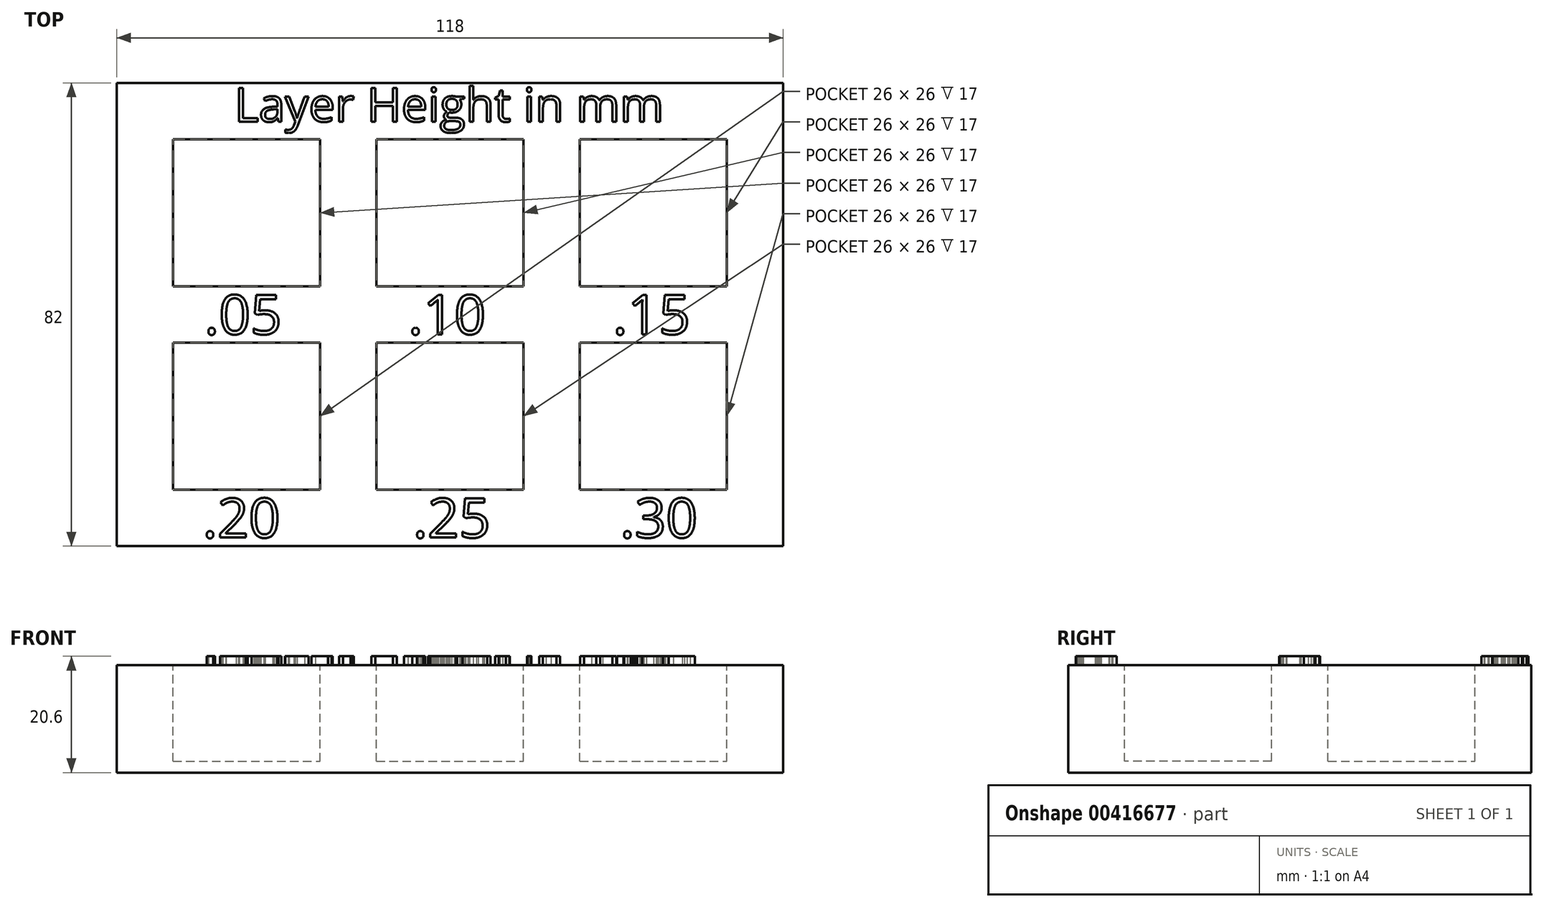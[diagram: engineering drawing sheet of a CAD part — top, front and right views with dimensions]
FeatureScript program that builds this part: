
annotation { "Feature Type Name" : "Feature", "Feature Type Description" : "" }
export const myFeature = defineFeature(function(context is Context, id is Id, definition is map)
    precondition{}
    {
        {
            var Q0;
            Q0=qCreatedBy(makeId("Top.planeOp"),FACE);
            var sketch = newSketch(context, id + "F0", { "sketchPlane" : qUnion([Q0])});
            skLineSegment(sketch, "E0.bottom", {"start": v(0, 0) * mm, "end": v(-118, 0) * mm});
            skLineSegment(sketch, "E0.top", {"start": v(0, 82) * mm, "end": v(-118, 82) * mm});
            skLineSegment(sketch, "E0.left", {"start": v(0, 0) * mm, "end": v(0, 82) * mm});
            skLineSegment(sketch, "E0.right", {"start": v(-118, 0) * mm, "end": v(-118, 82) * mm});
            skLineSegment(sketch, "E1.bottom", {"start": v(-108, 36) * mm, "end": v(-82, 36) * mm});
            skLineSegment(sketch, "E1.top", {"start": v(-108, 10) * mm, "end": v(-82, 10) * mm});
            skLineSegment(sketch, "E1.left", {"start": v(-108, 36) * mm, "end": v(-108, 10) * mm});
            skLineSegment(sketch, "E1.right", {"start": v(-82, 36) * mm, "end": v(-82, 10) * mm});
            skLineSegment(sketch, "E2.bottom", {"start": v(-72, 36) * mm, "end": v(-46, 36) * mm});
            skLineSegment(sketch, "E2.top", {"start": v(-72, 10) * mm, "end": v(-46, 10) * mm});
            skLineSegment(sketch, "E2.left", {"start": v(-72, 36) * mm, "end": v(-72, 10) * mm});
            skLineSegment(sketch, "E2.right", {"start": v(-46, 36) * mm, "end": v(-46, 10) * mm});
            skLineSegment(sketch, "E3.bottom", {"start": v(-36, 36) * mm, "end": v(-10, 36) * mm});
            skLineSegment(sketch, "E3.top", {"start": v(-36, 10) * mm, "end": v(-10, 10) * mm});
            skLineSegment(sketch, "E3.left", {"start": v(-36, 36) * mm, "end": v(-36, 10) * mm});
            skLineSegment(sketch, "E3.right", {"start": v(-10, 36) * mm, "end": v(-10, 10) * mm});
            skLineSegment(sketch, "E4", {"start": v(-118, 41) * mm, "end": v(0, 41) * mm, "construction": true});
            skLineSegment(sketch, "E5.MirrorCS", {"start": v(-72, 72) * mm, "end": v(-46, 72) * mm});
            skLineSegment(sketch, "E6.MirrorCS", {"start": v(-72, 46) * mm, "end": v(-72, 72) * mm});
            skLineSegment(sketch, "E7.MirrorCS", {"start": v(-46, 46) * mm, "end": v(-46, 72) * mm});
            skLineSegment(sketch, "E8.MirrorCS", {"start": v(-36, 46) * mm, "end": v(-10, 46) * mm});
            skLineSegment(sketch, "E9.MirrorCS", {"start": v(-10, 46) * mm, "end": v(-10, 72) * mm});
            skLineSegment(sketch, "E10.MirrorCS", {"start": v(-72, 46) * mm, "end": v(-46, 46) * mm});
            skLineSegment(sketch, "E11.MirrorCS", {"start": v(-108, 46) * mm, "end": v(-82, 46) * mm});
            skLineSegment(sketch, "E12.MirrorCS", {"start": v(-108, 72) * mm, "end": v(-82, 72) * mm});
            skLineSegment(sketch, "E13.MirrorCS", {"start": v(-108, 46) * mm, "end": v(-108, 72) * mm});
            skLineSegment(sketch, "E14.MirrorCS", {"start": v(-82, 46) * mm, "end": v(-82, 72) * mm});
            skLineSegment(sketch, "E15.MirrorCS", {"start": v(-36, 46) * mm, "end": v(-36, 72) * mm});
            skLineSegment(sketch, "E16.MirrorCS", {"start": v(-36, 72) * mm, "end": v(-10, 72) * mm});
            skSolve(sketch);
        }
        {
            var Q0;
            Q0=qSketchRegion(id+"F0",true);
            var Q1;
            Q1=makeQuery(id+"F0.imprint","IMPRINT",FACE,{"disambiguationData":[TD([[makeQuery(id+"F0.imprint","IMPRINT",EDGE,{"derivedFrom":sQuery(id+"F0.wireOp",EDGE,"fw1BMiOP-wDFj-6qkJ-aGuG-6Idq0dSNkA1F.bottom")}),-1.0]])]});
            var Q2;
            Q2=makeQuery(id+"F0.imprint","IMPRINT",FACE,{"disambiguationData":[TD([[makeQuery(id+"F0.imprint","IMPRINT",EDGE,{"derivedFrom":sQuery(id+"F0.wireOp",EDGE,"E1.bottom")}),-1.0]])]});
            var Q3;
            Q3=makeQuery(id+"F0.imprint","IMPRINT",FACE,{"disambiguationData":[TD([[makeQuery(id+"F0.imprint","IMPRINT",EDGE,{"derivedFrom":sQuery(id+"F0.wireOp",EDGE,"E2.bottom")}),-1.0]])]});
            var Q4;
            Q4=makeQuery(id+"F0.imprint","IMPRINT",FACE,{"disambiguationData":[TD([[makeQuery(id+"F0.imprint","IMPRINT",EDGE,{"derivedFrom":sQuery(id+"F0.wireOp",EDGE,"E3.bottom")}),-1.0]])]});
            var Q5;
            Q5=makeQuery(id+"F0.imprint","IMPRINT",FACE,{"disambiguationData":[TD([[makeQuery(id+"F0.imprint","IMPRINT",EDGE,{"derivedFrom":sQuery(id+"F0.wireOp",EDGE,"E11.MirrorCS")}),1.0]])]});
            var Q6;
            Q6=makeQuery(id+"F0.imprint","IMPRINT",FACE,{"disambiguationData":[TD([[makeQuery(id+"F0.imprint","IMPRINT",EDGE,{"derivedFrom":sQuery(id+"F0.wireOp",EDGE,"E5.MirrorCS")}),-1.0]])]});
            var Q7;
            Q7=makeQuery(id+"F0.imprint","IMPRINT",FACE,{"disambiguationData":[TD([[makeQuery(id+"F0.imprint","IMPRINT",EDGE,{"derivedFrom":sQuery(id+"F0.wireOp",EDGE,"E8.MirrorCS")}),1.0]])]});
            extrude(context, id + "F1", {"entities" : qUnion([Q0, Q1, Q2, Q3, Q4, Q5, Q6, Q7]), "oppositeDirection" : true, "depth" : 19 * mm});
        }
        {
            var Q0;
            Q0=makeQuery(id+"F0.imprint","IMPRINT",FACE,{"disambiguationData":[TD([[makeQuery(id+"F0.imprint","IMPRINT",EDGE,{"derivedFrom":sQuery(id+"F0.wireOp",EDGE,"fw1BMiOP-wDFj-6qkJ-aGuG-6Idq0dSNkA1F.bottom")}),-1.0]])]});
            var Q1;
            Q1=makeQuery(id+"F0.imprint","IMPRINT",FACE,{"disambiguationData":[TD([[makeQuery(id+"F0.imprint","IMPRINT",EDGE,{"derivedFrom":sQuery(id+"F0.wireOp",EDGE,"E1.bottom")}),-1.0]])]});
            var Q2;
            Q2=makeQuery(id+"F0.imprint","IMPRINT",FACE,{"disambiguationData":[TD([[makeQuery(id+"F0.imprint","IMPRINT",EDGE,{"derivedFrom":sQuery(id+"F0.wireOp",EDGE,"E2.bottom")}),-1.0]])]});
            var Q3;
            Q3=makeQuery(id+"F0.imprint","IMPRINT",FACE,{"disambiguationData":[TD([[makeQuery(id+"F0.imprint","IMPRINT",EDGE,{"derivedFrom":sQuery(id+"F0.wireOp",EDGE,"E3.bottom")}),-1.0]])]});
            var Q4;
            Q4=makeQuery(id+"F0.imprint","IMPRINT",FACE,{"disambiguationData":[TD([[makeQuery(id+"F0.imprint","IMPRINT",EDGE,{"derivedFrom":sQuery(id+"F0.wireOp",EDGE,"E11.MirrorCS")}),1.0]])]});
            var Q5;
            Q5=makeQuery(id+"F0.imprint","IMPRINT",FACE,{"disambiguationData":[TD([[makeQuery(id+"F0.imprint","IMPRINT",EDGE,{"derivedFrom":sQuery(id+"F0.wireOp",EDGE,"E5.MirrorCS")}),-1.0]])]});
            var Q6;
            Q6=makeQuery(id+"F0.imprint","IMPRINT",FACE,{"disambiguationData":[TD([[makeQuery(id+"F0.imprint","IMPRINT",EDGE,{"derivedFrom":sQuery(id+"F0.wireOp",EDGE,"E8.MirrorCS")}),1.0]])]});
            extrude(context, id + "F2", {"entities" : qUnion([Q0, Q1, Q2, Q3, Q4, Q5, Q6]), "operationType" : NewBodyOperationType.REMOVE, "oppositeDirection" : true, "depth" : 17 * mm});
        }
        {
            var Q0;
            Q0=makeQuery(id+"F0.imprint","IMPRINT",FACE,{"disambiguationData":[TD([[makeQuery(id+"F0.imprint","IMPRINT",EDGE,{"derivedFrom":sQuery(id+"F0.wireOp",EDGE,"E0.bottom")}),-1.0]])]});
            var sketch = newSketch(context, id + "F3", { "sketchPlane" : qUnion([Q0])});
            skText(sketch, "E17", { "text": "Layer Height in mm", "fontName": "OpenSans-Regular.ttf"});
            skText(sketch, "E18", { "text": ".05", "fontName": "OpenSans-Regular.ttf"});
            skText(sketch, "E19", { "text": ".10", "fontName": "OpenSans-Regular.ttf"});
            skText(sketch, "E20", { "text": ".15", "fontName": "OpenSans-Regular.ttf"});
            skText(sketch, "E21", { "text": ".20", "fontName": "OpenSans-Regular.ttf"});
            skText(sketch, "E22", { "text": ".25", "fontName": "OpenSans-Regular.ttf"});
            skText(sketch, "E23", { "text": ".30", "fontName": "OpenSans-Regular.ttf"});
            skLineSegment(sketch, "E24", {"start": v(-117.78, 5) * mm, "end": v(0, 5) * mm, "construction": true});
            const initialGuessF3  = {"E17": [-0.09714, 0.07513, 1, 0, 0.006], "E18": [-0.10247, 0.0375, 1, 0, 0.007], "E19": [-0.06637, 0.0375, 1, 0, 0.007], "E20": [-0.03015, 0.0375, 1, 0, 0.007], "E21": [-0.10276, 0.0015, 1, 0, 0.007], "E22": [-0.06553, 0.0015, 1, 0, 0.007], "E23": [-0.02887, 0.0015, 1, 0, 0.007]};
            skSetInitialGuess(sketch, initialGuessF3);
            skSolve(sketch);
        }
        {
            var Q0;
            Q0=qSketchRegion(id+"F3",true);
            extrude(context, id + "F4", {"entities" : qUnion([Q0]), "operationType" : NewBodyOperationType.ADD, "depth" : 1.6 * mm});
        }
    });
